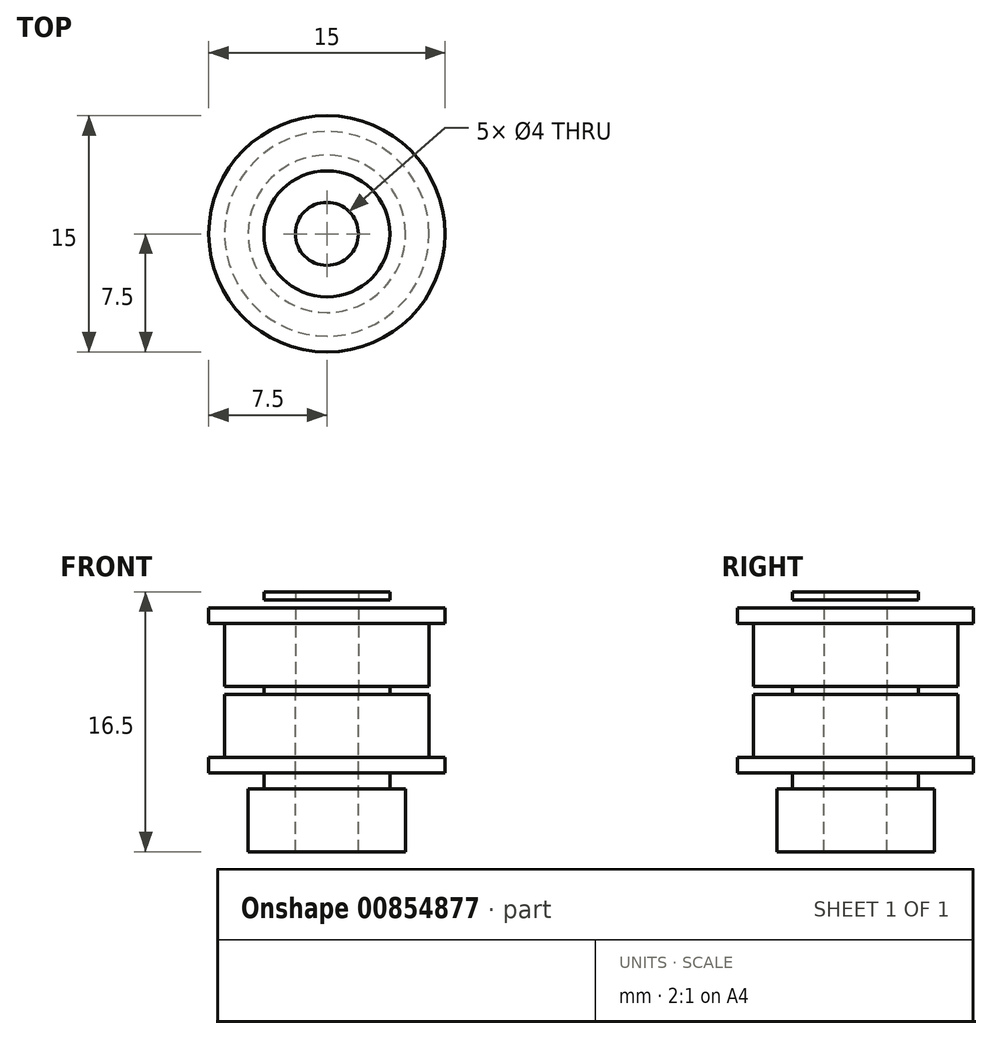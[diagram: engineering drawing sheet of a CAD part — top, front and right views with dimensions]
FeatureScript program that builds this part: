
annotation { "Feature Type Name" : "Feature", "Feature Type Description" : "" }
export const myFeature = defineFeature(function(context is Context, id is Id, definition is map)
    precondition{}
    {
        {
            var Q0;
            Q0=qCreatedBy(makeId("Top.planeOp"),FACE);
            var sketch = newSketch(context, id + "F0", { "sketchPlane" : qUnion([Q0])});
            skCircle(sketch, "E0", {"center": v(0, 0) * mm, "radius": 2 * mm});
            skCircle(sketch, "E1", {"center": v(0, 0) * mm, "radius": 4 * mm});
            skSolve(sketch);
        }
        {
            var Q0;
            Q0 = qSketchRegion(id + "F0", true);
            extrude(context, id + "F1", {"entities" : qUnion([Q0]), "depth" : 0.25 * mm, "offsetDistance" : 25 * mm, "hasSecondDirection" : true, "secondDirectionOppositeDirection" : true, "secondDirectionDepth" : 0.25 * mm});
        }
        {
            var Q0;
            Q0=makeQuery(id+"F1.opExtrude","CAP_FACE",FACE,{"disambiguationData":[OSD([sQuery(id+"F0.wireOp",EDGE,"E0"),sQuery(id+"F0.wireOp",EDGE,"E1")])],"isStart":false});
            var sketch = newSketch(context, id + "F2", { "sketchPlane" : qUnion([Q0])});
            skCircle(sketch, "E2.0", {"center": v(0, 0) * mm, "radius": 2 * mm});
            skCircle(sketch, "E3", {"center": v(0, 0) * mm, "radius": 6.5 * mm});
            skSolve(sketch);
        }
        {
            var Q0;
            Q0 = qSketchRegion(id + "F2", true);
            extrude(context, id + "F3", {"entities" : qUnion([Q0]), "depth" : 4 * mm, "offsetDistance" : 25 * mm});
        }
        {
            var Q0;
            Q0=makeQuery(id+"F3.opExtrude","CAP_FACE",FACE,{"disambiguationData":[OSD([sQuery(id+"F2.wireOp",EDGE,"E2.0"),sQuery(id+"F2.wireOp",EDGE,"E3")])],"isStart":false});
            var sketch = newSketch(context, id + "F4", { "sketchPlane" : qUnion([Q0])});
            skCircle(sketch, "E4.0", {"center": v(0, 0) * mm, "radius": 2 * mm});
            skCircle(sketch, "E5", {"center": v(0, 0) * mm, "radius": 7.5 * mm});
            skSolve(sketch);
        }
        {
            var Q0;
            Q0 = qSketchRegion(id + "F4", true);
            extrude(context, id + "F5", {"entities" : qUnion([Q0]), "operationType" : NewBodyOperationType.ADD, "depth" : 1 * mm, "offsetDistance" : 25 * mm});
        }
        {
            var Q0;
            Q0=makeQuery(id+"F1.opExtrude","SWEPT_BODY",BODY,{"disambiguationData":[OSD([sQuery(id+"F0.wireOp",EDGE,"E0"),sQuery(id+"F0.wireOp",EDGE,"E1")])]});
            transform(context, id + "F6", {"entities" : qUnion([Q0]), "transformType" : TransformType.TRANSLATION_3D, "dx" : 0 * mm, "dy" : 0 * mm, "dz" : 6 * mm, "makeCopy" : true});
        }
        {
            var Q0;
            Q0=makeQuery(id+"F3.opExtrude","SWEPT_BODY",BODY,{"disambiguationData":[OSD([sQuery(id+"F2.wireOp",EDGE,"E2.0"),sQuery(id+"F2.wireOp",EDGE,"E3")])]});
            var Q1;
            Q1=qCreatedBy(makeId("Top.planeOp"),FACE);
            mirror(context, id + "F7", {"entities" : qUnion([Q0]), "mirrorPlane" : qUnion([Q1])});
        }
        {
            var Q0;
            Q0=makeQuery(id+"F7.opPattern","COPY",FACE,{"derivedFrom":makeQuery(id+"F5.opExtrude","CAP_FACE",FACE,{"disambiguationData":[OSD([sQuery(id+"F4.wireOp",EDGE,"E4.0"),sQuery(id+"F4.wireOp",EDGE,"E5")])],"isStart":false}),"instanceName":"1"});
            var sketch = newSketch(context, id + "F8", { "sketchPlane" : qUnion([Q0])});
            skCircle(sketch, "E6.0", {"center": v(0, 0) * mm, "radius": 2 * mm});
            skCircle(sketch, "E7.0", {"center": v(0, 0) * mm, "radius": 4 * mm});
            skSolve(sketch);
        }
        {
            var Q0;
            Q0 = qSketchRegion(id + "F8", true);
            extrude(context, id + "F9", {"entities" : qUnion([Q0]), "depth" : 1 * mm, "offsetDistance" : 25 * mm});
        }
        {
            var Q0;
            Q0=makeQuery(id+"F9.opExtrude","CAP_FACE",FACE,{"disambiguationData":[OSD([sQuery(id+"F8.wireOp",EDGE,"E6.0"),sQuery(id+"F8.wireOp",EDGE,"E7.0")])],"isStart":false});
            var sketch = newSketch(context, id + "F10", { "sketchPlane" : qUnion([Q0])});
            skCircle(sketch, "E8.0", {"center": v(0, 0) * mm, "radius": 2 * mm});
            skCircle(sketch, "E9", {"center": v(0, 0) * mm, "radius": 5 * mm});
            skSolve(sketch);
        }
        {
            var Q0;
            Q0 = qSketchRegion(id + "F10", true);
            extrude(context, id + "F11", {"entities" : qUnion([Q0]), "operationType" : NewBodyOperationType.ADD, "depth" : 4 * mm, "offsetDistance" : 25 * mm});
        }
    });
